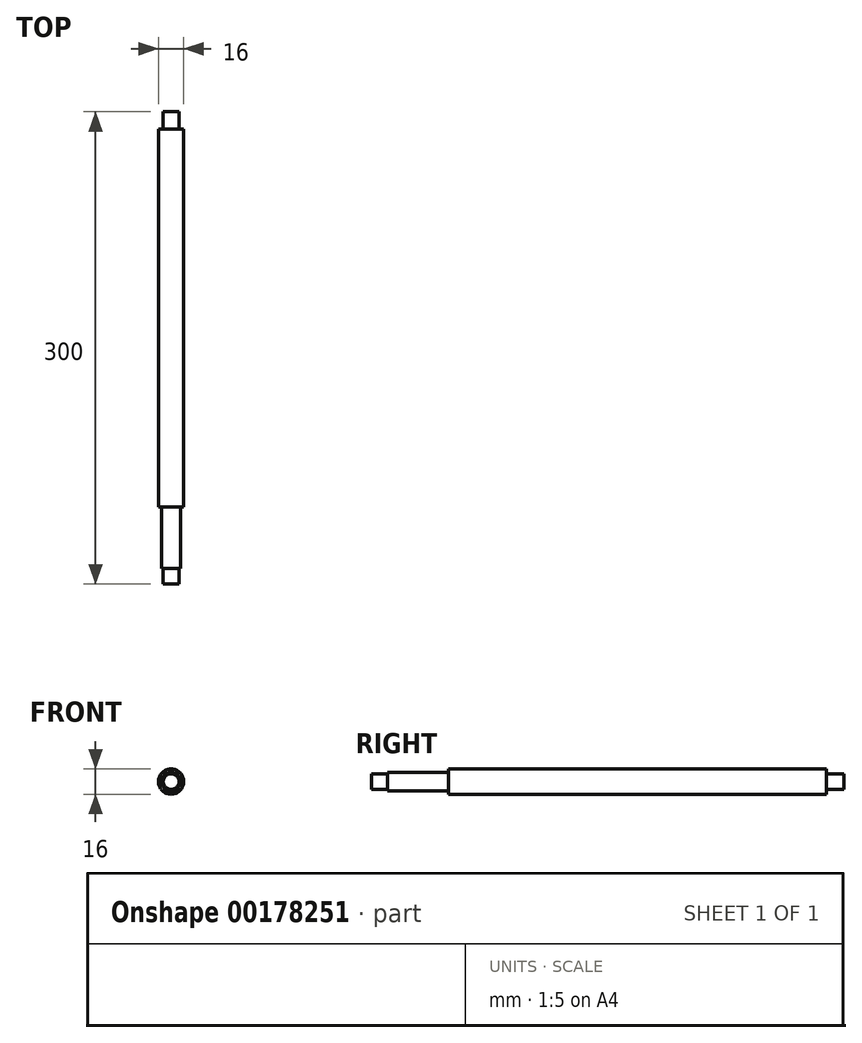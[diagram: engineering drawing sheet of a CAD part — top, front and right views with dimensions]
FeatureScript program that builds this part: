
annotation { "Feature Type Name" : "Feature", "Feature Type Description" : "" }
export const myFeature = defineFeature(function(context is Context, id is Id, definition is map)
    precondition{}
    {
        {
            var Q0;
            Q0=qCreatedBy(makeId("Front.planeOp"),FACE);
            var sketch = newSketch(context, id + "F0", { "sketchPlane" : qUnion([Q0])});
            skCircle(sketch, "E0", {"center": v(0, 0) * mm, "radius": 5 * mm});
            skSolve(sketch);
        }
        {
            var Q0;
            Q0=qSketchRegion(id+"F0",true);
            extrude(context, id + "F1", {"entities" : qUnion([Q0]), "depth" : 11 * mm});
        }
        {
            var Q0;
            Q0=makeQuery(id+"F1.opExtrude","CAP_FACE",FACE,{"disambiguationData":[OSD([sQuery(id+"F0.wireOp",EDGE,"E0")])],"isStart":false});
            var sketch = newSketch(context, id + "F2", { "sketchPlane" : qUnion([Q0])});
            skCircle(sketch, "E1", {"center": v(0, 0) * mm, "radius": 8 * mm});
            skSolve(sketch);
        }
        {
            var Q0;
            Q0=qSketchRegion(id+"F2",true);
            extrude(context, id + "F3", {"entities" : qUnion([Q0]), "operationType" : NewBodyOperationType.ADD, "depth" : 240 * mm});
        }
        {
            var Q0;
            Q0=makeQuery(id+"F3.opExtrude","CAP_FACE",FACE,{"disambiguationData":[OSD([sQuery(id+"F2.wireOp",EDGE,"E1")])],"isStart":false});
            var sketch = newSketch(context, id + "F4", { "sketchPlane" : qUnion([Q0])});
            skCircle(sketch, "E2", {"center": v(0, 0) * mm, "radius": 6 * mm});
            skSolve(sketch);
        }
        {
            var Q0;
            Q0=qSketchRegion(id+"F4",true);
            extrude(context, id + "F5", {"entities" : qUnion([Q0]), "operationType" : NewBodyOperationType.ADD, "depth" : 39 * mm});
        }
        {
            var Q0;
            Q0=makeQuery(id+"F5.opExtrude","CAP_FACE",FACE,{"disambiguationData":[OSD([sQuery(id+"F4.wireOp",EDGE,"E2")])],"isStart":false});
            var sketch = newSketch(context, id + "F6", { "sketchPlane" : qUnion([Q0])});
            skCircle(sketch, "E3", {"center": v(0, 0) * mm, "radius": 5 * mm});
            skSolve(sketch);
        }
        {
            var Q0;
            Q0=qSketchRegion(id+"F6",true);
            extrude(context, id + "F7", {"entities" : qUnion([Q0]), "operationType" : NewBodyOperationType.ADD, "depth" : 10 * mm});
        }
    });
